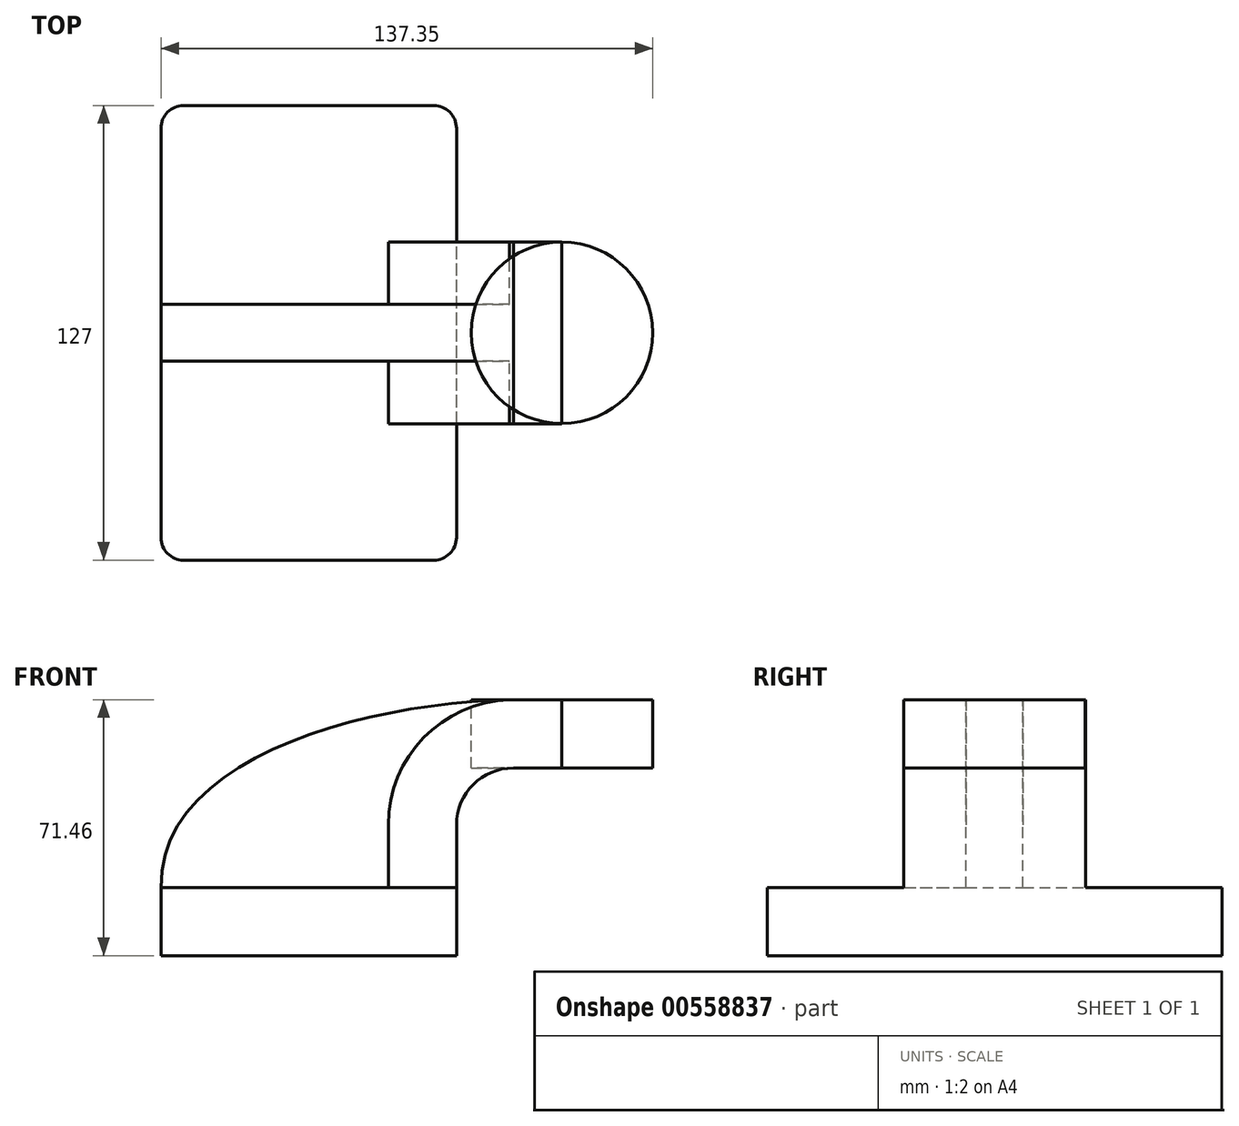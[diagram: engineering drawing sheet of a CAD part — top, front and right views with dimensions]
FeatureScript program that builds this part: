
annotation { "Feature Type Name" : "Feature", "Feature Type Description" : "" }
export const myFeature = defineFeature(function(context is Context, id is Id, definition is map)
    precondition{}
    {
        {
            var Q0;
            Q0=qCreatedBy(makeId("Front.planeOp"),FACE);
            var sketch = newSketch(context, id + "F0", { "sketchPlane" : qUnion([Q0])});
            skLineSegment(sketch, "E0.bottom", {"start": v(-41.28, 9.52) * mm, "end": v(41.27, 9.53) * mm});
            skLineSegment(sketch, "E0.top", {"start": v(-41.28, -9.53) * mm, "end": v(41.28, -9.53) * mm});
            skLineSegment(sketch, "E0.left", {"start": v(-41.28, 9.52) * mm, "end": v(-41.27, -9.53) * mm});
            skLineSegment(sketch, "E0.right", {"start": v(41.28, 9.53) * mm, "end": v(41.28, -9.52) * mm});
            skPoint(sketch, "E0.middle", {"position": v(0, 0) * mm});
            skLineSegment(sketch, "E1.bottom", {"start": v(70.72, 66.68) * mm, "end": v(121.52, 66.68) * mm});
            skLineSegment(sketch, "E1.top", {"start": v(70.72, 38.1) * mm, "end": v(121.52, 38.1) * mm});
            skLineSegment(sketch, "E1.left", {"start": v(70.72, 66.68) * mm, "end": v(70.72, 38.1) * mm});
            skLineSegment(sketch, "E1.right", {"start": v(121.52, 66.68) * mm, "end": v(121.52, 38.1) * mm});
            skPoint(sketch, "E1.middle", {"position": v(96.12, 52.39) * mm});
            skLineSegment(sketch, "E2", {"start": v(41.27, 9.53) * mm, "end": v(41.27, 27) * mm});
            skArc(sketch, "E3", {"start": v(41.27, 27) * mm, "mid": v(45.92, 38.23) * mm, "end": v(57.15, 42.88) * mm});
            skLineSegment(sketch, "E4", {"start": v(57.15, 42.88) * mm, "end": v(96.07, 42.88) * mm});
            skLineSegment(sketch, "E5.0", {"start": v(57.15, 61.93) * mm, "end": v(96.07, 61.93) * mm});
            skArc(sketch, "E5.1", {"start": v(22.22, 27) * mm, "mid": v(32.45, 51.7) * mm, "end": v(57.15, 61.93) * mm});
            skLineSegment(sketch, "E5.2", {"start": v(22.22, 9.53) * mm, "end": v(22.22, 27) * mm});
            skLineSegment(sketch, "E6", {"start": v(96.07, 61.93) * mm, "end": v(96.07, 38.1) * mm});
            skLineSegment(sketch, "E7", {"start": v(96.07, 61.93) * mm, "end": v(96.07, 66.68) * mm});
            skFitSpline(sketch, "E8", {"points": [v(-41.28, 9.52) * mm, v(57.15, 61.93) * mm], "startDerivative": vector(-1.7, 110.77) * mm, "endDerivative": vector(117.79, 1.37) * mm});
            skSolve(sketch);
        }
        {
            var Q0;
            Q0=makeQuery(id+"F0.imprint","IMPRINT",FACE,{"disambiguationData":[TD([[makeQuery(id+"F0.imprint","IMPRINT",EDGE,{"derivedFrom":sQuery(id+"F0.wireOp",EDGE,"E0.top")}),1.0]])]});
            extrude(context, id + "F1", {"entities" : qUnion([Q0]), "endBound" : BoundingType.SYMMETRIC, "depth" : 127 * mm, "offsetDistance" : 25.4 * mm});
        }
        {
            var Q0;
            {var subQ1=sQuery(id+"F0.wireOp",EDGE,"E2");Q0=makeQuery(id+"F0.imprint","IMPRINT",FACE,{"disambiguationData":[TD([[makeQuery(id+"F0.imprint","IMPRINT",EDGE,{"derivedFrom":subQ1}),1.0]])]});}
            extrude(context, id + "F2", {"entities" : qUnion([Q0]), "operationType" : NewBodyOperationType.ADD, "endBound" : BoundingType.SYMMETRIC, "depth" : 50.8 * mm, "offsetDistance" : 25.4 * mm});
        }
        {
            var Q0;
            {var subQ3=sQuery(id+"F0.wireOp",EDGE,"E5.2");Q0=makeQuery(id+"F0.imprint","IMPRINT",FACE,{"disambiguationData":[TD([[makeQuery(id+"F0.imprint","IMPRINT",EDGE,{"derivedFrom":subQ3}),1.0]])]});}
            extrude(context, id + "F3", {"entities" : qUnion([Q0]), "operationType" : NewBodyOperationType.ADD, "endBound" : BoundingType.SYMMETRIC, "depth" : 15.88 * mm, "offsetDistance" : 25.4 * mm});
        }
        {
            var Q0;
            {var subQ0=sQuery(id+"F0.wireOp",EDGE,"E5.0");var subQ1=sQuery(id+"F0.wireOp",EDGE,"E1.left");var subQ2=makeQuery(id+"F0.imprint","INTERSECT",VERTEX,{"derivedFrom":[subQ1,subQ0]});Q0=makeQuery(id+"F0.imprint","IMPRINT",FACE,{"disambiguationData":[TD([[makeQuery(id+"F0.imprint","IMPRINT",EDGE,{"disambiguationData":[TD([[subQ2,-1.0]])],"derivedFrom":subQ1}),1.0]])]});}
            var Q1;
            Q1=sQuery(id+"F0.wireOp",EDGE,"E1.left");
            revolve(context, id + "F4", {"entities" : qUnion([Q0]), "axis" : qUnion([Q1]), "revolveType" : RevolveType.FULL});
        }
        {
            var Q0;
            Q0=makeQuery(id+"F1.opExtrude","CAP_EDGE",EDGE,{"disambiguationData":[OSD([sQuery(id+"F0.wireOp",EDGE,"E0.right")])],"isStart":false});
            var Q1;
            Q1=makeQuery(id+"F1.opExtrude","CAP_EDGE",EDGE,{"disambiguationData":[OSD([sQuery(id+"F0.wireOp",EDGE,"E0.right")])],"isStart":true});
            var Q2;
            Q2=makeQuery(id+"F1.opExtrude","CAP_EDGE",EDGE,{"disambiguationData":[OSD([sQuery(id+"F0.wireOp",EDGE,"E0.left")])],"isStart":false});
            var Q3;
            Q3=makeQuery(id+"F1.opExtrude","CAP_EDGE",EDGE,{"disambiguationData":[OSD([sQuery(id+"F0.wireOp",EDGE,"E0.left")])],"isStart":true});
            fillet(context, id + "F5", {"entities" : qUnion([Q0, Q1, Q2, Q3]), "radius" : 6.35 * mm, "tangentPropagation" : true, "allowEdgeOverflow" : false});
        }
    });
